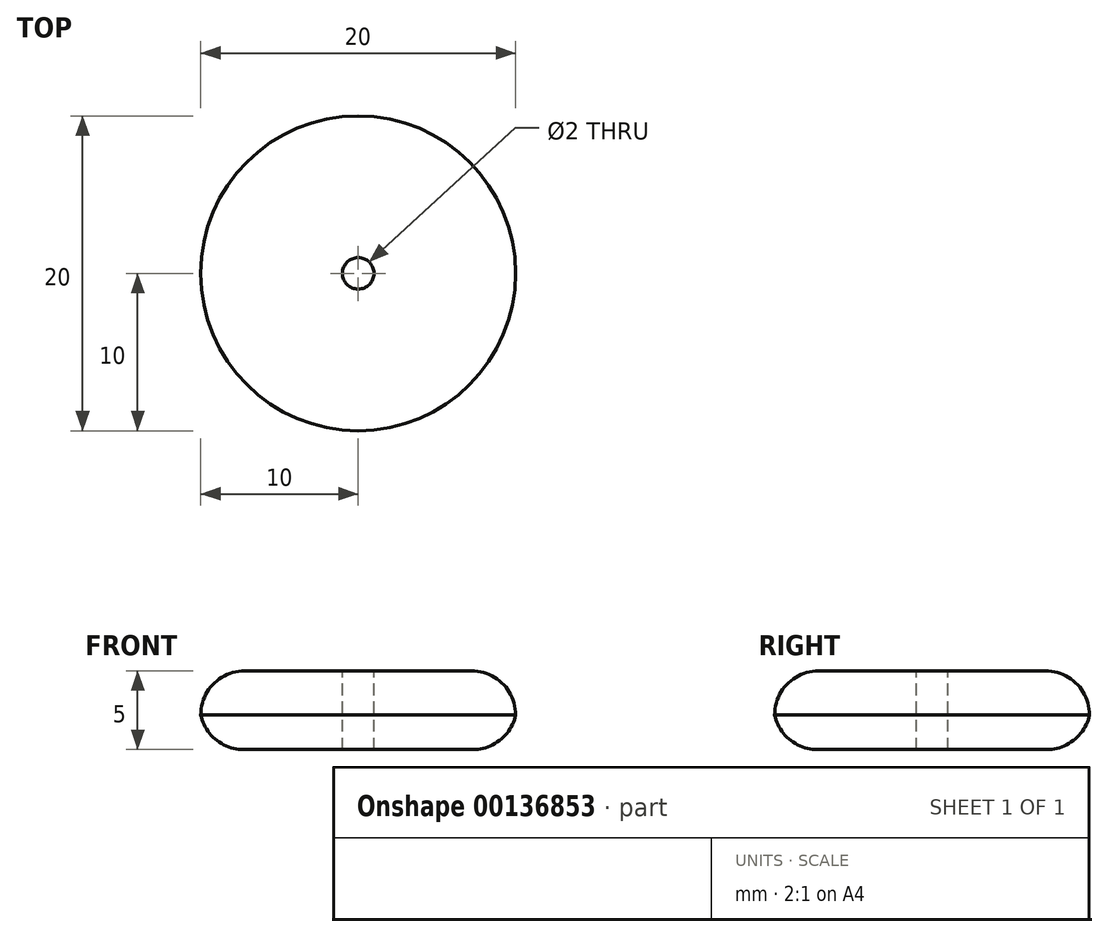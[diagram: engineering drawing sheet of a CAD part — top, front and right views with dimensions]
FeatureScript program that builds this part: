
annotation { "Feature Type Name" : "Feature", "Feature Type Description" : "" }
export const myFeature = defineFeature(function(context is Context, id is Id, definition is map)
    precondition{}
    {
        {
            var Q0;
            Q0=qCreatedBy(makeId("Front.planeOp"),FACE);
            var sketch = newSketch(context, id + "F0", { "sketchPlane" : qUnion([Q0])});
            skLineSegment(sketch, "E0.bottom", {"start": v(10, -2.5) * mm, "end": v(-1, -2.5) * mm});
            skLineSegment(sketch, "E0.top", {"start": v(10, 2.5) * mm, "end": v(0, 2.5) * mm});
            skLineSegment(sketch, "E0.left", {"start": v(10, -2.5) * mm, "end": v(10, 2.5) * mm});
            skPoint(sketch, "E0.middle", {"position": v(0, 0) * mm});
            skLineSegment(sketch, "E1.bottom", {"start": v(8.5, -2.5) * mm, "end": v(0, -2.5) * mm});
            skLineSegment(sketch, "E1.top", {"start": v(8.5, 2.5) * mm, "end": v(0, 2.5) * mm});
            skLineSegment(sketch, "E2.bottom", {"start": v(1, -2.5) * mm, "end": v(0, -2.5) * mm});
            skLineSegment(sketch, "E2.top", {"start": v(1, 2.5) * mm, "end": v(0, 2.5) * mm});
            skLineSegment(sketch, "E2.left", {"start": v(1, -2.5) * mm, "end": v(1, 2.5) * mm});
            skPoint(sketch, "E3.orphan", {"position": v(-8.5, -2.5) * mm});
            skPoint(sketch, "E4.orphan", {"position": v(-8.5, 2.5) * mm});
            skPoint(sketch, "E5.trimOffspring.end.orphan", {"position": v(-10, 2.5) * mm});
            skPoint(sketch, "E6.trimOffspring.end.orphan", {"position": v(-10, -2.5) * mm});
            skLineSegment(sketch, "E7", {"start": v(0, 2.5) * mm, "end": v(0, -2.5) * mm});
            skPoint(sketch, "E8.orphan", {"position": v(-1, 2.5) * mm});
            skSolve(sketch);
        }
        {
            var Q0;
            Q0=makeQuery(id+"F0.imprint","IMPRINT",FACE,{"disambiguationData":[TD([[makeQuery(id+"F0.imprint","IMPRINT",EDGE,{"derivedFrom":sQuery(id+"F0.wireOp",EDGE,"E0.top")}),1.0]])]});
            var Q1;
            Q1=sQuery(id+"F0.wireOp",EDGE,"E7");
            revolve(context, id + "F1", {"entities" : qUnion([Q0]), "axis" : qUnion([Q1]), "revolveType" : RevolveType.FULL});
        }
        {
            var Q0;
            Q0=makeQuery(id+"F1.opRevolve","SWEPT_EDGE",EDGE,{"disambiguationData":[OSD([sQuery(id+"F0.wireOp",EDGE,"E0.top"),sQuery(id+"F0.wireOp",EDGE,"E0.left")])]});
            fillet(context, id + "F2", {"entities" : qUnion([Q0]), "radius" : 2.8 * mm, "tangentPropagation" : true, "allowEdgeOverflow" : false});
        }
        {
            var Q0;
            Q0=makeQuery(id+"F1.opRevolve","SWEPT_EDGE",EDGE,{"disambiguationData":[OSD([sQuery(id+"F0.wireOp",EDGE,"E0.bottom"),sQuery(id+"F0.wireOp",EDGE,"E0.left")])]});
            fillet(context, id + "F3", {"entities" : qUnion([Q0]), "radius" : 2.8 * mm, "tangentPropagation" : true, "allowEdgeOverflow" : false});
        }
    });
